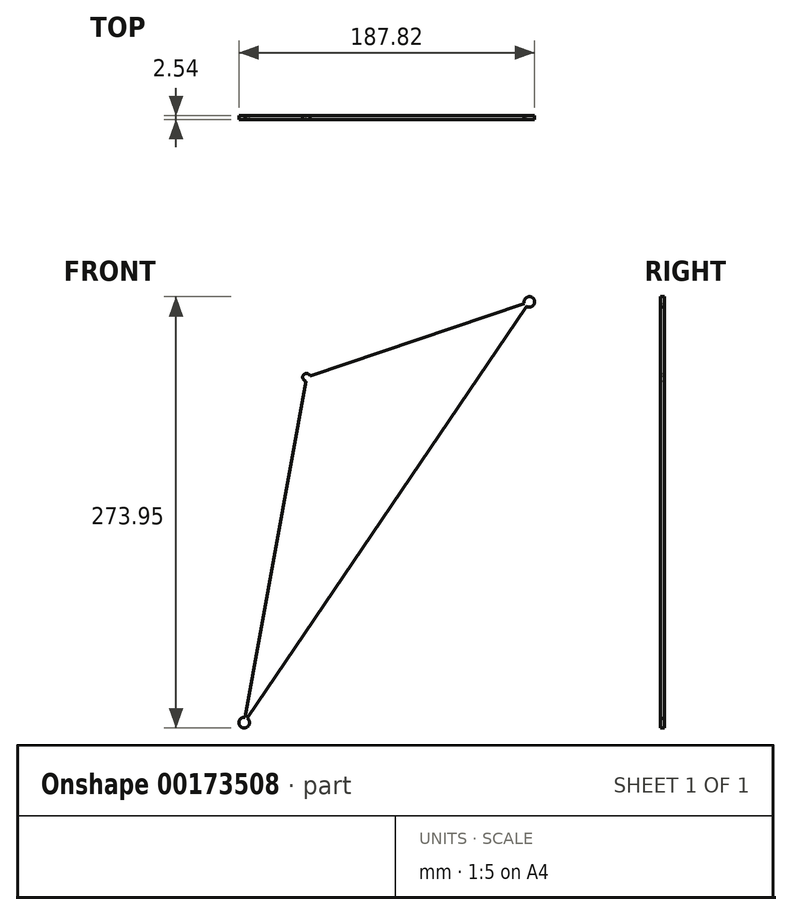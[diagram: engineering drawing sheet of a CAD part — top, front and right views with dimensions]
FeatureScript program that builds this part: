
annotation { "Feature Type Name" : "Feature", "Feature Type Description" : "" }
export const myFeature = defineFeature(function(context is Context, id is Id, definition is map)
    precondition{}
    {
        {
            var Q0;
            Q0=qCreatedBy(makeId("Front.planeOp"),FACE);
            var sketch = newSketch(context, id + "F0", { "sketchPlane" : qUnion([Q0])});
            skCircle(sketch, "E0", {"center": v(-148.04, -2.75) * mm, "radius": 2.41 * mm});
            skLineSegment(sketch, "E1", {"start": v(-6.52, 45.08) * mm, "end": v(-148.04, -2.75) * mm});
            skLineSegment(sketch, "E2", {"start": v(-148.04, -2.75) * mm, "end": v(-187.62, -222.14) * mm});
            skLineSegment(sketch, "E3", {"start": v(-187.62, -222.14) * mm, "end": v(-6.52, 45.08) * mm});
            skCircle(sketch, "E4", {"center": v(-6.52, 45.08) * mm, "radius": 3.37 * mm});
            skCircle(sketch, "E5", {"center": v(-187.62, -222.14) * mm, "radius": 3.37 * mm});
            skSolve(sketch);
        }
        {
            var Q0;
            {var subQ6=sQuery(id+"F0.wireOp",EDGE,"E0");var subQ9=sQuery(id+"F0.wireOp",EDGE,"E1");var subQ10=makeQuery(id+"F0.imprint","INTERSECT",VERTEX,{"derivedFrom":[subQ6,subQ9]});Q0=makeQuery(id+"F0.imprint","IMPRINT",FACE,{"disambiguationData":[TD([[makeQuery(id+"F0.imprint","IMPRINT",EDGE,{"disambiguationData":[TD([[subQ10,1.0]])],"derivedFrom":subQ6}),-1.0]])]});}
            var Q1;
            {var subQ0=sQuery(id+"F0.wireOp",EDGE,"E3");var subQ1=sQuery(id+"F0.wireOp",EDGE,"E1");var subQ2=makeQuery(id+"F0.imprint","INTERSECT",VERTEX,{"derivedFrom":[subQ1,subQ0]});Q1=makeQuery(id+"F0.imprint","IMPRINT",FACE,{"disambiguationData":[TD([[makeQuery(id+"F0.imprint","IMPRINT",EDGE,{"disambiguationData":[TD([[subQ2,-1.0]])],"derivedFrom":subQ1}),-1.0]])]});}
            var Q2;
            {var subQ0=sQuery(id+"F0.wireOp",EDGE,"E3");var subQ1=sQuery(id+"F0.wireOp",EDGE,"E1");var subQ2=makeQuery(id+"F0.imprint","INTERSECT",VERTEX,{"derivedFrom":[subQ1,subQ0]});Q2=makeQuery(id+"F0.imprint","IMPRINT",FACE,{"disambiguationData":[TD([[makeQuery(id+"F0.imprint","IMPRINT",EDGE,{"disambiguationData":[TD([[subQ2,-1.0]])],"derivedFrom":subQ1}),1.0]])]});}
            var Q3;
            {var subQ0=sQuery(id+"F0.wireOp",EDGE,"E1");var subQ1=sQuery(id+"F0.wireOp",EDGE,"E0");var subQ2=makeQuery(id+"F0.imprint","INTERSECT",VERTEX,{"derivedFrom":[subQ1,subQ0]});Q3=makeQuery(id+"F0.imprint","IMPRINT",FACE,{"disambiguationData":[TD([[makeQuery(id+"F0.imprint","IMPRINT",EDGE,{"disambiguationData":[TD([[subQ2,1.0]])],"derivedFrom":subQ1}),1.0]])]});}
            var Q4;
            {var subQ0=sQuery(id+"F0.wireOp",EDGE,"E1");var subQ1=sQuery(id+"F0.wireOp",EDGE,"E0");var subQ2=makeQuery(id+"F0.imprint","INTERSECT",VERTEX,{"derivedFrom":[subQ1,subQ0]});Q4=makeQuery(id+"F0.imprint","IMPRINT",FACE,{"disambiguationData":[TD([[makeQuery(id+"F0.imprint","IMPRINT",EDGE,{"disambiguationData":[TD([[subQ2,-1.0]])],"derivedFrom":subQ1}),1.0]])]});}
            var Q5;
            {var subQ0=sQuery(id+"F0.wireOp",EDGE,"E3");var subQ1=sQuery(id+"F0.wireOp",EDGE,"E2");var subQ2=makeQuery(id+"F0.imprint","INTERSECT",VERTEX,{"derivedFrom":[subQ1,subQ0]});Q5=makeQuery(id+"F0.imprint","IMPRINT",FACE,{"disambiguationData":[TD([[makeQuery(id+"F0.imprint","IMPRINT",EDGE,{"disambiguationData":[TD([[subQ2,1.0]])],"derivedFrom":subQ1}),-1.0]])]});}
            var Q6;
            {var subQ0=sQuery(id+"F0.wireOp",EDGE,"E3");var subQ1=sQuery(id+"F0.wireOp",EDGE,"E2");var subQ2=makeQuery(id+"F0.imprint","INTERSECT",VERTEX,{"derivedFrom":[subQ1,subQ0]});Q6=makeQuery(id+"F0.imprint","IMPRINT",FACE,{"disambiguationData":[TD([[makeQuery(id+"F0.imprint","IMPRINT",EDGE,{"disambiguationData":[TD([[subQ2,1.0]])],"derivedFrom":subQ1}),1.0]])]});}
            extrude(context, id + "F1", {"entities" : qUnion([Q0, Q1, Q2, Q3, Q4, Q5, Q6]), "depth" : 2.54 * mm});
        }
    });
